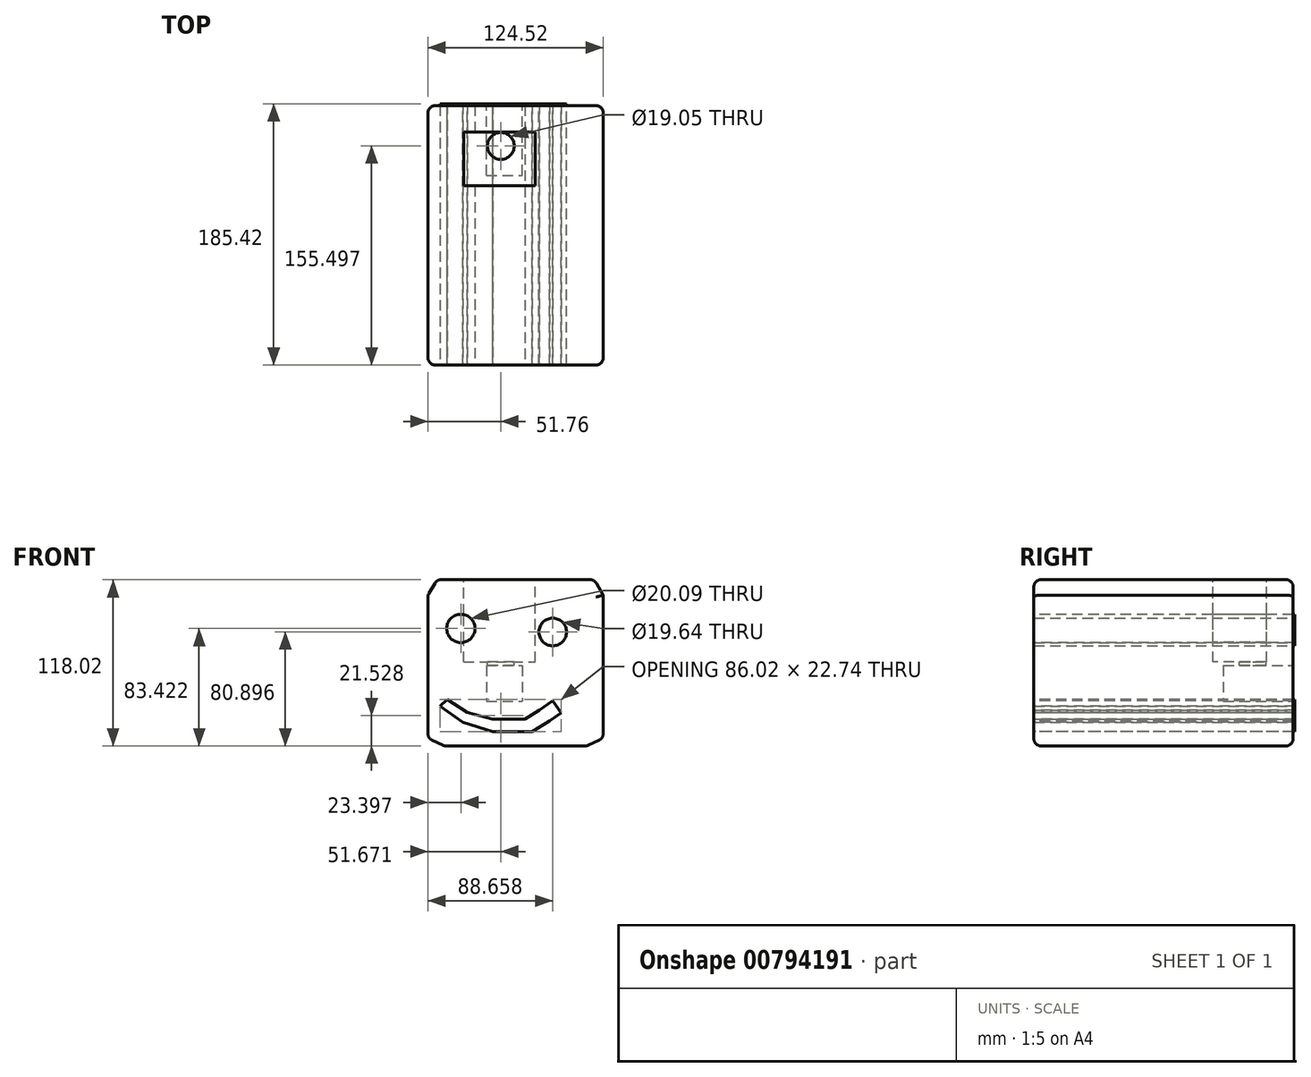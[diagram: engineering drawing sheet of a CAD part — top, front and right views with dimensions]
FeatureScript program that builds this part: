
annotation { "Feature Type Name" : "Feature", "Feature Type Description" : "" }
export const myFeature = defineFeature(function(context is Context, id is Id, definition is map)
    precondition{}
    {
        {
            var Q0;
            Q0=qCreatedBy(makeId("Front.planeOp"),FACE);
            var sketch = newSketch(context, id + "F0", { "sketchPlane" : qUnion([Q0])});
            skLineSegment(sketch, "E0", {"start": v(-40.3, -36.95) * mm, "end": v(61.3, -36.95) * mm});
            skLineSegment(sketch, "E1", {"start": v(61.3, -36.95) * mm, "end": v(72.76, -31.48) * mm});
            skLineSegment(sketch, "E2", {"start": v(-40.3, -36.95) * mm, "end": v(-51.76, -31.48) * mm});
            skLineSegment(sketch, "E3", {"start": v(-51.76, -31.48) * mm, "end": v(-51.76, 70.12) * mm});
            skLineSegment(sketch, "E4", {"start": v(72.76, -31.48) * mm, "end": v(72.76, 70.12) * mm});
            skLineSegment(sketch, "E5", {"start": v(-51.76, 70.12) * mm, "end": v(-45.32, 81.07) * mm});
            skLineSegment(sketch, "E6", {"start": v(72.76, 70.12) * mm, "end": v(66.32, 81.07) * mm});
            skLineSegment(sketch, "E7", {"start": v(-45.32, 81.07) * mm, "end": v(66.32, 81.07) * mm});
            skCircle(sketch, "E8", {"center": v(-28.36, 46.47) * mm, "radius": 10.04 * mm});
            skCircle(sketch, "E9", {"center": v(36.9, 43.95) * mm, "radius": 9.82 * mm});
            skLineSegment(sketch, "E10", {"start": v(-38.05, -4.05) * mm, "end": v(-23.73, -13.32) * mm});
            skLineSegment(sketch, "E11", {"start": v(-23.73, -13.32) * mm, "end": v(-6.05, -17.95) * mm});
            skLineSegment(sketch, "E12", {"start": v(-6.05, -17.95) * mm, "end": v(17.1, -17.95) * mm});
            skLineSegment(sketch, "E13", {"start": v(17.1, -17.95) * mm, "end": v(27.21, -11.63) * mm});
            skLineSegment(sketch, "E14", {"start": v(27.21, -11.63) * mm, "end": v(36.9, -4.9) * mm});
            skLineSegment(sketch, "E15", {"start": v(36.9, -4.9) * mm, "end": v(42.92, -13.56) * mm});
            skLineSegment(sketch, "E16", {"start": v(42.92, -13.56) * mm, "end": v(34.68, -19.29) * mm});
            skLineSegment(sketch, "E17", {"start": v(34.68, -19.29) * mm, "end": v(22.16, -26.79) * mm});
            skLineSegment(sketch, "E18", {"start": v(22.16, -26.79) * mm, "end": v(-5.63, -26.79) * mm});
            skLineSegment(sketch, "E19", {"start": v(-5.63, -26.79) * mm, "end": v(-27.1, -20.05) * mm});
            skLineSegment(sketch, "E20", {"start": v(-27.1, -20.05) * mm, "end": v(-43.1, -8.68) * mm});
            skLineSegment(sketch, "E21", {"start": v(-43.1, -8.68) * mm, "end": v(-38.05, -4.05) * mm});
            skLineSegment(sketch, "E22.bottom", {"start": v(-10.26, 20.08) * mm, "end": v(15.14, 20.08) * mm});
            skLineSegment(sketch, "E22.top", {"start": v(-10.26, -5.32) * mm, "end": v(15.14, -5.32) * mm});
            skLineSegment(sketch, "E22.left", {"start": v(-10.26, 20.08) * mm, "end": v(-10.26, -5.32) * mm});
            skLineSegment(sketch, "E22.right", {"start": v(15.14, 20.08) * mm, "end": v(15.14, -5.32) * mm});
            skSolve(sketch);
        }
        {
            var Q0;
            Q0 = qSketchRegion(id + "F0", true);
            extrude(context, id + "F1", {"entities" : qUnion([Q0]), "depth" : 184.15 * mm, "offsetDistance" : 25.4 * mm});
        }
        {
            var Q0;
            Q0=makeQuery(id+"F1.opExtrude","CAP_EDGE",EDGE,{"disambiguationData":[OSD([sQuery(id+"F0.wireOp",EDGE,"E6")])],"isStart":true});
            var Q1;
            Q1=makeQuery(id+"F1.opExtrude","CAP_EDGE",EDGE,{"disambiguationData":[OSD([sQuery(id+"F0.wireOp",EDGE,"E7")])],"isStart":true});
            var Q2;
            Q2=makeQuery(id+"F1.opExtrude","CAP_EDGE",EDGE,{"disambiguationData":[OSD([sQuery(id+"F0.wireOp",EDGE,"E5")])],"isStart":true});
            var Q3;
            Q3=makeQuery(id+"F1.opExtrude","CAP_EDGE",EDGE,{"disambiguationData":[OSD([sQuery(id+"F0.wireOp",EDGE,"E3")])],"isStart":true});
            var Q4;
            Q4=makeQuery(id+"F1.opExtrude","CAP_EDGE",EDGE,{"disambiguationData":[OSD([sQuery(id+"F0.wireOp",EDGE,"E2")])],"isStart":true});
            var Q5;
            Q5=makeQuery(id+"F1.opExtrude","CAP_EDGE",EDGE,{"disambiguationData":[OSD([sQuery(id+"F0.wireOp",EDGE,"E0")])],"isStart":true});
            var Q6;
            Q6=makeQuery(id+"F1.opExtrude","CAP_EDGE",EDGE,{"disambiguationData":[OSD([sQuery(id+"F0.wireOp",EDGE,"E1")])],"isStart":true});
            var Q7;
            Q7=makeQuery(id+"F1.opExtrude","CAP_EDGE",EDGE,{"disambiguationData":[OSD([sQuery(id+"F0.wireOp",EDGE,"E4")])],"isStart":true});
            var Q8;
            Q8=makeQuery(id+"F1.opExtrude","SWEPT_EDGE",EDGE,{"disambiguationData":[OSD([sQuery(id+"F0.wireOp",EDGE,"E3"),sQuery(id+"F0.wireOp",EDGE,"E5")])]});
            var Q9;
            Q9=makeQuery(id+"F1.opExtrude","SWEPT_EDGE",EDGE,{"disambiguationData":[OSD([sQuery(id+"F0.wireOp",EDGE,"E5"),sQuery(id+"F0.wireOp",EDGE,"E7")])]});
            var Q10;
            Q10=makeQuery(id+"F1.opExtrude","SWEPT_EDGE",EDGE,{"disambiguationData":[OSD([sQuery(id+"F0.wireOp",EDGE,"E2"),sQuery(id+"F0.wireOp",EDGE,"E3")])]});
            var Q11;
            Q11=makeQuery(id+"F1.opExtrude","SWEPT_EDGE",EDGE,{"disambiguationData":[OSD([sQuery(id+"F0.wireOp",EDGE,"E0"),sQuery(id+"F0.wireOp",EDGE,"E2")])]});
            var Q12;
            Q12=makeQuery(id+"F1.opExtrude","CAP_EDGE",EDGE,{"disambiguationData":[OSD([sQuery(id+"F0.wireOp",EDGE,"E2")])],"isStart":false});
            var Q13;
            Q13=makeQuery(id+"F1.opExtrude","CAP_EDGE",EDGE,{"disambiguationData":[OSD([sQuery(id+"F0.wireOp",EDGE,"E3")])],"isStart":false});
            var Q14;
            Q14=makeQuery(id+"F1.opExtrude","CAP_EDGE",EDGE,{"disambiguationData":[OSD([sQuery(id+"F0.wireOp",EDGE,"E5")])],"isStart":false});
            var Q15;
            Q15=makeQuery(id+"F1.opExtrude","SWEPT_EDGE",EDGE,{"disambiguationData":[OSD([sQuery(id+"F0.wireOp",EDGE,"E1"),sQuery(id+"F0.wireOp",EDGE,"E4")])]});
            var Q16;
            Q16=makeQuery(id+"F1.opExtrude","CAP_EDGE",EDGE,{"disambiguationData":[OSD([sQuery(id+"F0.wireOp",EDGE,"E0")])],"isStart":false});
            var Q17;
            Q17=makeQuery(id+"F1.opExtrude","CAP_EDGE",EDGE,{"disambiguationData":[OSD([sQuery(id+"F0.wireOp",EDGE,"E1")])],"isStart":false});
            var Q18;
            Q18=makeQuery(id+"F1.opExtrude","CAP_EDGE",EDGE,{"disambiguationData":[OSD([sQuery(id+"F0.wireOp",EDGE,"E4")])],"isStart":false});
            var Q19;
            Q19=makeQuery(id+"F1.opExtrude","CAP_EDGE",EDGE,{"disambiguationData":[OSD([sQuery(id+"F0.wireOp",EDGE,"E7")])],"isStart":false});
            var Q20;
            Q20=makeQuery(id+"F1.opExtrude","CAP_EDGE",EDGE,{"disambiguationData":[OSD([sQuery(id+"F0.wireOp",EDGE,"E6")])],"isStart":false});
            var Q21;
            Q21=makeQuery(id+"F1.opExtrude","SWEPT_EDGE",EDGE,{"disambiguationData":[OSD([sQuery(id+"F0.wireOp",EDGE,"E6"),sQuery(id+"F0.wireOp",EDGE,"E7")])]});
            var Q22;
            Q22=makeQuery(id+"F1.opExtrude","SWEPT_EDGE",EDGE,{"disambiguationData":[OSD([sQuery(id+"F0.wireOp",EDGE,"E0"),sQuery(id+"F0.wireOp",EDGE,"E1")])]});
            fillet(context, id + "F2", {"entities" : qUnion([Q0, Q1, Q2, Q3, Q4, Q5, Q6, Q7, Q8, Q9, Q10, Q11, Q12, Q13, Q14, Q15, Q16, Q17, Q18, Q19, Q20, Q21, Q22]), "radius" : 5.08 * mm, "tangentPropagation" : true, "allowEdgeOverflow" : false});
        }
        {
            var Q0;
            Q0=makeQuery(id+"F1.opExtrude","CAP_FACE",FACE,{"disambiguationData":[OSD([sQuery(id+"F0.wireOp",EDGE,"E0"),sQuery(id+"F0.wireOp",EDGE,"E1"),sQuery(id+"F0.wireOp",EDGE,"E2"),sQuery(id+"F0.wireOp",EDGE,"E3"),sQuery(id+"F0.wireOp",EDGE,"E4"),sQuery(id+"F0.wireOp",EDGE,"E5"),sQuery(id+"F0.wireOp",EDGE,"E6"),sQuery(id+"F0.wireOp",EDGE,"E7")])],"isStart":false});
            var sketch = newSketch(context, id + "F3", { "sketchPlane" : qUnion([Q0])});
            skSolve(sketch);
        }
        {
            var Q0;
            Q0=makeQuery(id+"F3.imprint","IMPRINT",FACE,{"disambiguationData":[TD([[makeQuery(id+"F3.imprint","IMPRINT",EDGE,{"derivedFrom":makeQuery(id+"F1.opExtrude","CAP_EDGE",EDGE,{"disambiguationData":[OSD([sQuery(id+"F0.wireOp",EDGE,"E8")])],"isStart":false})}),1.0]])]});
            var Q1;
            Q1=makeQuery(id+"F3.imprint","IMPRINT",FACE,{"disambiguationData":[TD([[makeQuery(id+"F3.imprint","IMPRINT",EDGE,{"derivedFrom":makeQuery(id+"F1.opExtrude","CAP_EDGE",EDGE,{"disambiguationData":[OSD([sQuery(id+"F0.wireOp",EDGE,"E9")])],"isStart":false})}),1.0]])]});
            var Q2;
            Q2=makeQuery(id+"F3.imprint","IMPRINT",FACE,{"disambiguationData":[TD([[makeQuery(id+"F3.imprint","IMPRINT",EDGE,{"derivedFrom":makeQuery(id+"F1.opExtrude","CAP_EDGE",EDGE,{"disambiguationData":[OSD([sQuery(id+"F0.wireOp",EDGE,"E10")])],"isStart":false})}),-1.0]])]});
            extrude(context, id + "F4", {"entities" : qUnion([Q0, Q1, Q2]), "oppositeDirection" : true, "depth" : 185.42 * mm, "offsetDistance" : 25.4 * mm});
        }
        {
            var Q0;
            Q0=makeQuery(id+"F1.opExtrude","CAP_FACE",FACE,{"disambiguationData":[OSD([sQuery(id+"F0.wireOp",EDGE,"E0"),sQuery(id+"F0.wireOp",EDGE,"E1"),sQuery(id+"F0.wireOp",EDGE,"E2"),sQuery(id+"F0.wireOp",EDGE,"E3"),sQuery(id+"F0.wireOp",EDGE,"E4"),sQuery(id+"F0.wireOp",EDGE,"E5"),sQuery(id+"F0.wireOp",EDGE,"E6"),sQuery(id+"F0.wireOp",EDGE,"E7"),sQuery(id+"F0.wireOp",EDGE,"E8"),sQuery(id+"F0.wireOp",EDGE,"E9"),sQuery(id+"F0.wireOp",EDGE,"E10"),sQuery(id+"F0.wireOp",EDGE,"E11"),sQuery(id+"F0.wireOp",EDGE,"E12"),sQuery(id+"F0.wireOp",EDGE,"E13"),sQuery(id+"F0.wireOp",EDGE,"E14"),sQuery(id+"F0.wireOp",EDGE,"E15"),sQuery(id+"F0.wireOp",EDGE,"E16"),sQuery(id+"F0.wireOp",EDGE,"E17"),sQuery(id+"F0.wireOp",EDGE,"E18"),sQuery(id+"F0.wireOp",EDGE,"E19"),sQuery(id+"F0.wireOp",EDGE,"E20"),sQuery(id+"F0.wireOp",EDGE,"E21"),sQuery(id+"F0.wireOp",EDGE,"E22.bottom"),sQuery(id+"F0.wireOp",EDGE,"E22.top"),sQuery(id+"F0.wireOp",EDGE,"E22.left"),sQuery(id+"F0.wireOp",EDGE,"E22.right")])],"isStart":false});
            var sketch = newSketch(context, id + "F5", { "sketchPlane" : qUnion([Q0])});
            skLineSegment(sketch, "E23", {"start": v(-10.26, 20.08) * mm, "end": v(-10.26, -5.32) * mm});
            skLineSegment(sketch, "E24", {"start": v(-10.26, -5.32) * mm, "end": v(15.14, -5.32) * mm});
            skLineSegment(sketch, "E25", {"start": v(15.14, -5.32) * mm, "end": v(15.14, 20.08) * mm});
            skLineSegment(sketch, "E26", {"start": v(15.14, 20.08) * mm, "end": v(-10.26, 20.08) * mm});
            skSolve(sketch);
        }
        {
            var Q0;
            Q0 = qSketchRegion(id + "F5", true);
            extrude(context, id + "F6", {"entities" : qUnion([Q0]), "operationType" : NewBodyOperationType.ADD, "oppositeDirection" : true, "depth" : 134.62 * mm, "offsetDistance" : 25.4 * mm});
        }
        {
            var Q0;
            Q0=makeQuery(id+"F1.opExtrude","SWEPT_FACE",FACE,{"disambiguationData":[OSD([sQuery(id+"F0.wireOp",EDGE,"E7")])]});
            var sketch = newSketch(context, id + "F7", { "sketchPlane" : qUnion([Q0])});
            skLineSegment(sketch, "E27.bottom", {"start": v(-26.45, -18.88) * mm, "end": v(24.35, -18.88) * mm});
            skLineSegment(sketch, "E27.top", {"start": v(-26.45, -56.98) * mm, "end": v(24.35, -56.98) * mm});
            skLineSegment(sketch, "E27.left", {"start": v(-26.45, -18.88) * mm, "end": v(-26.45, -56.98) * mm});
            skLineSegment(sketch, "E27.right", {"start": v(24.35, -18.88) * mm, "end": v(24.35, -56.98) * mm});
            skSolve(sketch);
        }
        {
            var Q0;
            Q0 = qSketchRegion(id + "F7", true);
            extrude(context, id + "F8", {"entities" : qUnion([Q0]), "operationType" : NewBodyOperationType.REMOVE, "oppositeDirection" : true, "depth" : 58.42 * mm, "offsetDistance" : 25.4 * mm});
        }
        {
            var Q0;
            Q0=makeQuery(id+"F8.boolean.opBoolean","COPY",FACE,{"derivedFrom":makeQuery(id+"F8.opExtrude","CAP_FACE",FACE,{"disambiguationData":[OSD([sQuery(id+"F7.wireOp",EDGE,"E27.bottom"),sQuery(id+"F7.wireOp",EDGE,"E27.top"),sQuery(id+"F7.wireOp",EDGE,"E27.left"),sQuery(id+"F7.wireOp",EDGE,"E27.right")])],"isStart":false})});
            var sketch = newSketch(context, id + "F9", { "sketchPlane" : qUnion([Q0])});
            skSolve(sketch);
        }
        {
            var Q0;
            Q0=makeQuery(id+"F9.imprint","IMPRINT",FACE,{"disambiguationData":[TD([[makeQuery(id+"F9.imprint","IMPRINT",EDGE,{"derivedFrom":makeQuery(id+"F8.boolean.opBoolean","COPY",EDGE,{"derivedFrom":makeQuery(id+"F8.opExtrude","CAP_EDGE",EDGE,{"disambiguationData":[OSD([sQuery(id+"F7.wireOp",EDGE,"E27.bottom")])],"isStart":false})})}),-1.0]])]});
            var sketch = newSketch(context, id + "F10", { "sketchPlane" : qUnion([Q0])});
            skCircle(sketch, "E28", {"center": v(0, -28.65) * mm, "radius": 9.53 * mm});
            skSolve(sketch);
        }
        {
            var Q0;
            Q0 = qSketchRegion(id + "F10", true);
            extrude(context, id + "F11", {"entities" : qUnion([Q0]), "operationType" : NewBodyOperationType.REMOVE, "oppositeDirection" : true, "depth" : 25.4 * mm, "offsetDistance" : 25.4 * mm});
        }
    });
